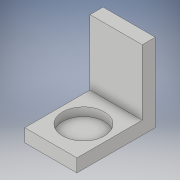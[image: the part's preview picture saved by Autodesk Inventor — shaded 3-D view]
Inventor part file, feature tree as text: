
AUTODESK INVENTOR PART (.ipt)
format: ipt  version: 2019 (Build 230136000, 136)  size: 109,568 bytes
history: native  units: in
note: dims shown in document units (in); Inventor stores cm internally (conversion verified against a paired STEP export)
features: sketch x2, extrude x1, hole x1, projected_geometry x1
ambient origin geometry x8: Origin, YZ Plane, XZ Plane, XY Plane, X Axis, Y Axis, Z Axis, Center Point
bodies: Solid1 (feature_tree)
feature tree (5):
  extrude  "Extrusion1"  Depth=0.75in
  hole  "Hole2"  [1 undecoded]
  sketch  "Sketch1"  dims[d0=0.125in d1=0.75in]
  sketch  "Sketch3"  dims[d4=0.125in d5=0.75in d6=0.5in d7=0.0in d15=0.4in d16=0.75in d17=0.375in d18=0.25in d19=0.5635in d20=0.08in d21=0.0in]
  projected_geometry  "Projected Loop2"
note: 1 required parameter value undecoded (feature->parameter linkage not recoverable at this tier; creation-order binding heuristic only, values carry confidence <= 0.55)
